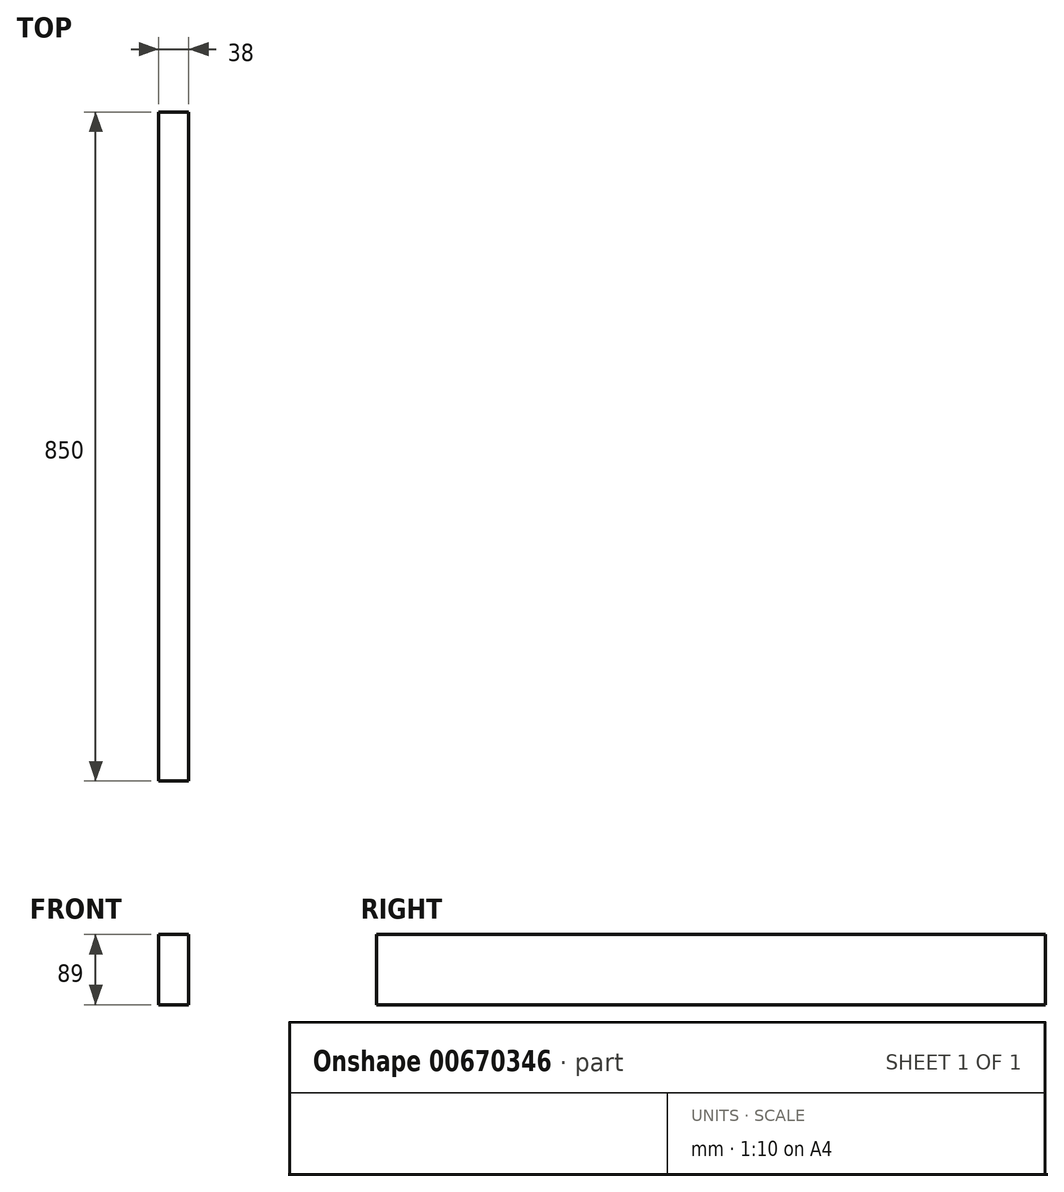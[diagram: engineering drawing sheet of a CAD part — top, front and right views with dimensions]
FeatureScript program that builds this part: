
annotation { "Feature Type Name" : "Feature", "Feature Type Description" : "" }
export const myFeature = defineFeature(function(context is Context, id is Id, definition is map)
    precondition{}
    {
        {
            var Q0;
            Q0=qCreatedBy(makeId("Front.planeOp"),FACE);
            var sketch = newSketch(context, id + "F0", { "sketchPlane" : qUnion([Q0])});
            skLineSegment(sketch, "E0.bottom", {"start": v(-19, 44.5) * mm, "end": v(19, 44.5) * mm});
            skLineSegment(sketch, "E0.top", {"start": v(-19, -44.5) * mm, "end": v(19, -44.5) * mm});
            skLineSegment(sketch, "E0.left", {"start": v(-19, 44.5) * mm, "end": v(-19, -44.5) * mm});
            skLineSegment(sketch, "E0.right", {"start": v(19, 44.5) * mm, "end": v(19, -44.5) * mm});
            skPoint(sketch, "E0.middle", {"position": v(0, 0) * mm});
            skSolve(sketch);
        }
        {
            var Q0;
            Q0=makeQuery(id+"F0.imprint","IMPRINT",FACE,{"disambiguationData":[TD([[makeQuery(id+"F0.imprint","IMPRINT",EDGE,{"derivedFrom":sQuery(id+"F0.wireOp",EDGE,"E0.bottom")}),-1.0]])]});
            extrude(context, id + "F1", {"entities" : qUnion([Q0]), "endBound" : BoundingType.SYMMETRIC, "depth" : 850 * mm, "offsetDistance" : 25 * mm});
        }
    });
